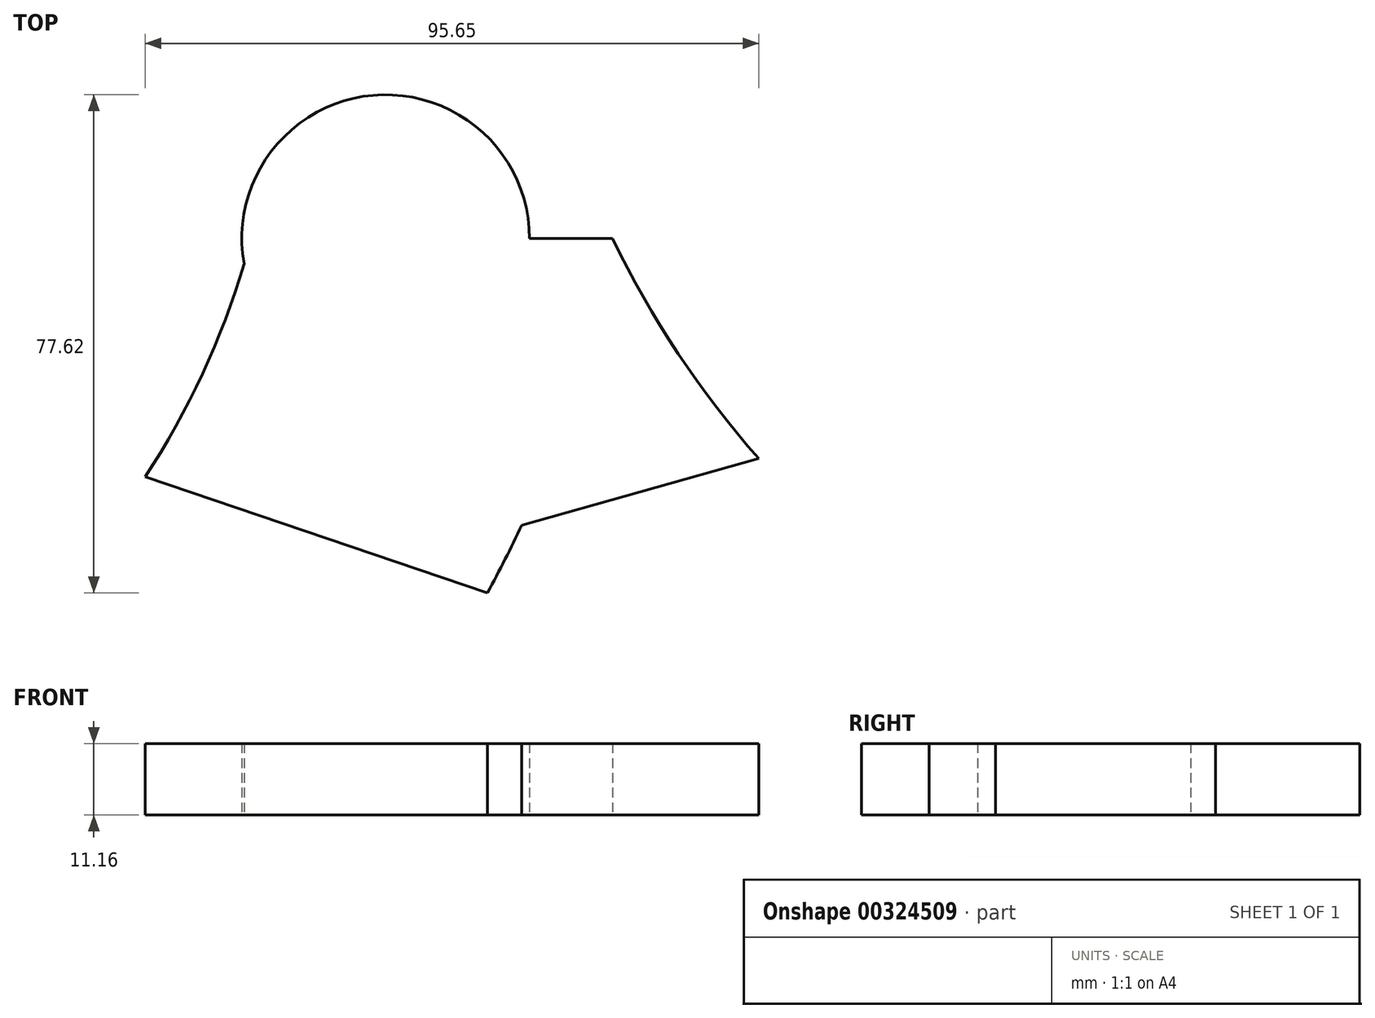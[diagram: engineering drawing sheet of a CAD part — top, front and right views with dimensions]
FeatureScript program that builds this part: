
annotation { "Feature Type Name" : "Feature", "Feature Type Description" : "" }
export const myFeature = defineFeature(function(context is Context, id is Id, definition is map)
    precondition{}
    {
        {
            var Q0;
            Q0=qCreatedBy(makeId("Front.planeOp"),FACE);
            var sketch = newSketch(context, id + "F0", { "sketchPlane" : qUnion([Q0])});
            skLineSegment(sketch, "E0.bottom", {"start": v(-27.01, 11.16) * mm, "end": v(29.31, 11.16) * mm});
            skLineSegment(sketch, "E0.top", {"start": v(-27.01, 0) * mm, "end": v(29.31, 0) * mm});
            skLineSegment(sketch, "E0.left", {"start": v(-27.01, 11.16) * mm, "end": v(-27.01, 0) * mm});
            skLineSegment(sketch, "E0.right", {"start": v(29.31, 11.16) * mm, "end": v(29.31, 0) * mm});
            skSolve(sketch);
        }
        {
            var Q0;
            Q0=qCreatedBy(makeId("Top.planeOp"),FACE);
            var sketch = newSketch(context, id + "F1", { "sketchPlane" : qUnion([Q0])});
            skArc(sketch, "E1", {"start": v(-23.65, -43.86) * mm, "mid": v(-13.05, -22.65) * mm, "end": v(-6.03, 0) * mm});
            skArc(sketch, "E2", {"start": v(-6.03, 0) * mm, "mid": v(4.53, -22.76) * mm, "end": v(18.1, -43.86) * mm});
            skCircle(sketch, "E3", {"center": v(-6.03, 0) * mm, "radius": 22.42 * mm});
            skSolve(sketch);
        }
        {
            var Q0;
            Q0=makeQuery(id+"F0.imprint","IMPRINT",FACE,{"disambiguationData":[TD([[makeQuery(id+"F0.imprint","IMPRINT",EDGE,{"derivedFrom":sQuery(id+"F0.wireOp",EDGE,"E0.bottom")}),-1.0]])]});
            var Q1;
            Q1=sQuery(id+"F1.wireOp",EDGE,"E1");
            sweep(context, id + "F2", {"profiles" : qUnion([Q0]), "path" : qUnion([Q1])});
        }
        {
            var Q0;
            Q0 = qSketchRegion(id + "F0", true);
            var Q1;
            Q1=sQuery(id+"F1.wireOp",EDGE,"E2");
            sweep(context, id + "F3", {"operationType" : NewBodyOperationType.ADD, "profiles" : qUnion([Q0]), "path" : qUnion([Q1])});
        }
        {
            var Q0;
            {var subQ0=sQuery(id+"F1.wireOp",EDGE,"E2");var subQ1=sQuery(id+"F1.wireOp",EDGE,"E1");var subQ2=makeQuery(id+"F1.imprint","INTERSECT",VERTEX,{"derivedFrom":[subQ1,subQ0]});Q0=makeQuery(id+"F1.imprint","IMPRINT",FACE,{"disambiguationData":[TD([[makeQuery(id+"F1.imprint","IMPRINT",EDGE,{"disambiguationData":[TD([[subQ2,1.0]])],"derivedFrom":subQ1}),1.0]])]});}
            var Q1;
            {var subQ0=sQuery(id+"F0.wireOp",EDGE,"E0.bottom");Q1=makeQuery(id+"F3.boolean.opBoolean","MERGE",FACE,{"derivedFrom":[makeQuery(id+"F2.opSweep","SWEPT_FACE",FACE,{"disambiguationData":[OSD([subQ0,sQuery(id+"F1.wireOp",EDGE,"E1")])]}),makeQuery(id+"F3.opSweep","SWEPT_FACE",FACE,{"disambiguationData":[OSD([subQ0,sQuery(id+"F1.wireOp",EDGE,"E2")])]})]});}
            extrude(context, id + "F4", {"entities" : qUnion([Q0]), "operationType" : NewBodyOperationType.ADD, "endBound" : BoundingType.UP_TO_SURFACE, "endBoundEntityFace" : qUnion([Q1]), "depth" : 25.4 * mm});
        }
    });
